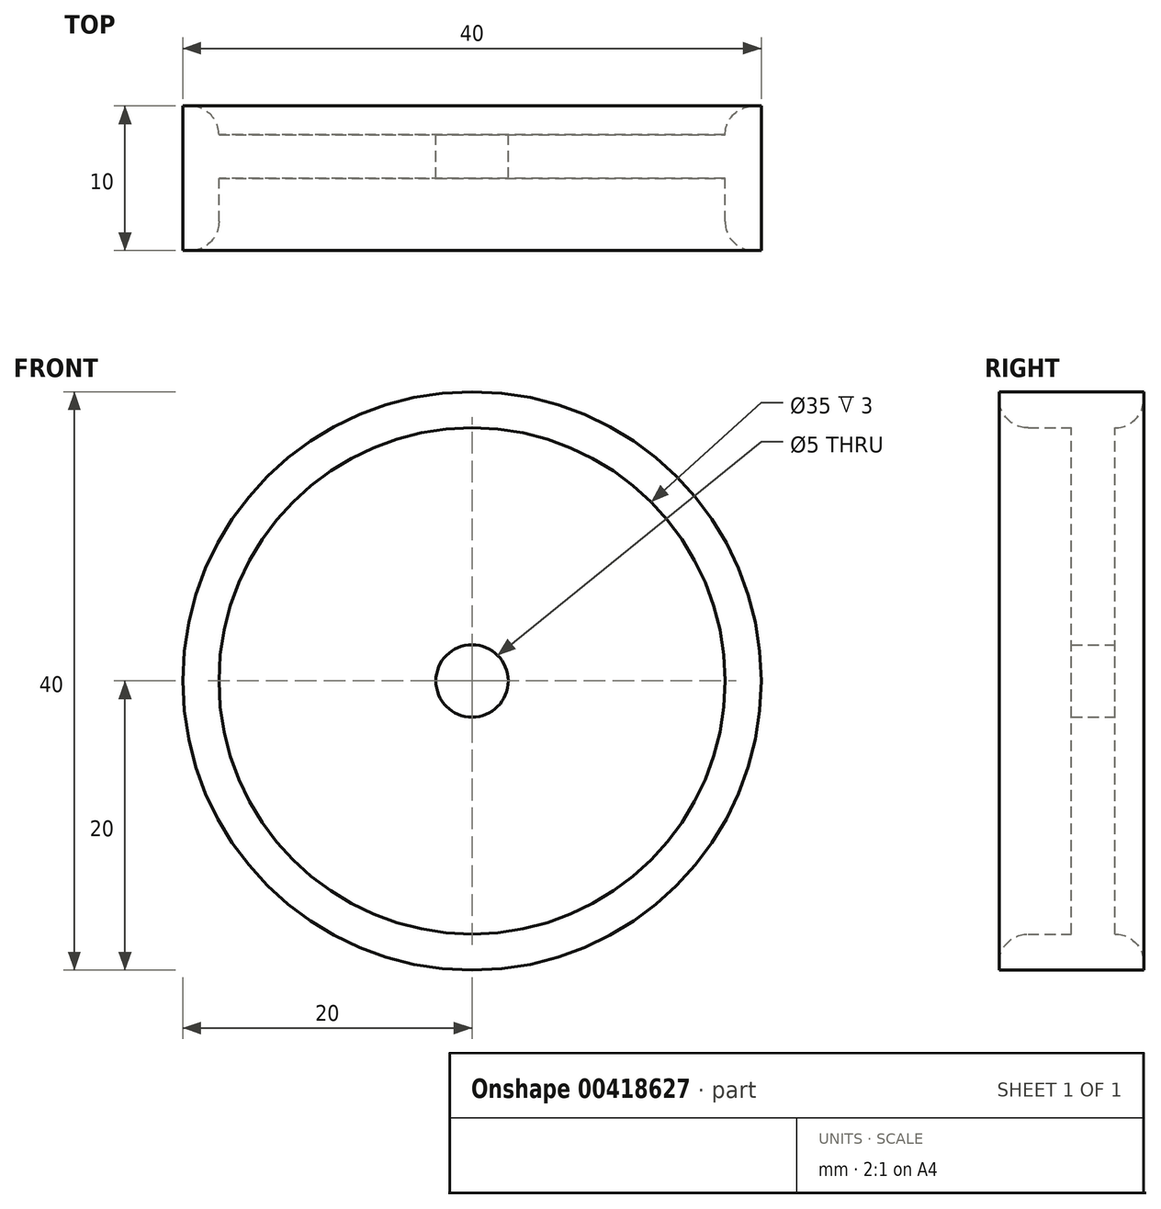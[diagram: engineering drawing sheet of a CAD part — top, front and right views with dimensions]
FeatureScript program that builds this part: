
annotation { "Feature Type Name" : "Feature", "Feature Type Description" : "" }
export const myFeature = defineFeature(function(context is Context, id is Id, definition is map)
    precondition{}
    {
        {
            var Q0;
            Q0=qCreatedBy(makeId("Front.planeOp"),FACE);
            var sketch = newSketch(context, id + "F0", { "sketchPlane" : qUnion([Q0])});
            skCircle(sketch, "E0", {"center": v(0, 0) * mm, "radius": 20 * mm});
            skCircle(sketch, "E1", {"center": v(0, 0) * mm, "radius": 17.5 * mm});
            skLineSegment(sketch, "E2", {"start": v(0, 0) * mm, "end": v(1.68, 17.42) * mm});
            skLineSegment(sketch, "E3.1.0", {"start": v(0, 0) * mm, "end": v(-17.42, 1.68) * mm});
            skLineSegment(sketch, "E3.2.0", {"start": v(0, 0) * mm, "end": v(-1.68, -17.42) * mm});
            skLineSegment(sketch, "E3.3.0", {"start": v(0, 0) * mm, "end": v(17.42, -1.68) * mm});
            skSolve(sketch);
        }
        {
            var Q0;
            Q0=makeQuery(id+"F0.imprint","IMPRINT",FACE,{"disambiguationData":[TD([[makeQuery(id+"F0.imprint","IMPRINT",EDGE,{"derivedFrom":sQuery(id+"F0.wireOp",EDGE,"E0")}),1.0]])]});
            extrude(context, id + "F1", {"entities" : qUnion([Q0]), "depth" : 10 * mm});
        }
        {
            var Q0;
            {var subQ0=sQuery(id+"F0.wireOp",EDGE,"E2");Q0=makeQuery(id+"F0.imprint","IMPRINT",FACE,{"disambiguationData":[TD([[makeQuery(id+"F0.imprint","IMPRINT",EDGE,{"derivedFrom":subQ0}),1.0]])]});}
            var Q1;
            {var subQ0=sQuery(id+"F0.wireOp",EDGE,"E3.2.0");Q1=makeQuery(id+"F0.imprint","IMPRINT",FACE,{"disambiguationData":[TD([[makeQuery(id+"F0.imprint","IMPRINT",EDGE,{"derivedFrom":subQ0}),1.0]])]});}
            var Q2;
            {var subQ0=sQuery(id+"F0.wireOp",EDGE,"E3.1.0");Q2=makeQuery(id+"F0.imprint","IMPRINT",FACE,{"disambiguationData":[TD([[makeQuery(id+"F0.imprint","IMPRINT",EDGE,{"derivedFrom":subQ0}),1.0]])]});}
            var Q3;
            {var subQ0=sQuery(id+"F0.wireOp",EDGE,"E2");Q3=makeQuery(id+"F0.imprint","IMPRINT",FACE,{"disambiguationData":[TD([[makeQuery(id+"F0.imprint","IMPRINT",EDGE,{"derivedFrom":subQ0}),-1.0]])]});}
            extrude(context, id + "F2", {"entities" : qUnion([Q0, Q1, Q2, Q3]), "operationType" : NewBodyOperationType.ADD, "depth" : 5 * mm, "hasSecondDirection" : true, "secondDirectionOppositeDirection" : true, "secondDirectionDepth" : -2 * mm});
        }
        {
            var Q0;
            Q0=makeQuery(id+"F1.opExtrude","CAP_EDGE",EDGE,{"disambiguationData":[OSD([sQuery(id+"F0.wireOp",EDGE,"E1")])],"isStart":false});
            var Q1;
            Q1=makeQuery(id+"F1.opExtrude","CAP_EDGE",EDGE,{"disambiguationData":[OSD([sQuery(id+"F0.wireOp",EDGE,"E1")])],"isStart":true});
            fillet(context, id + "F3", {"entities" : qUnion([Q0, Q1]), "radius" : 2 * mm, "tangentPropagation" : true, "allowEdgeOverflow" : false});
        }
        {
            var Q0;
            Q0=sQuery(id+"F0.wireOp",VERTEX,"E0.center");
            var Q1;
            Q1=makeQuery(id+"F1.opExtrude","SWEPT_BODY",BODY,{"disambiguationData":[OSD([sQuery(id+"F0.wireOp",EDGE,"E0"),sQuery(id+"F0.wireOp",EDGE,"E1")])]});
            hole(context, id + "F4", {"style" : HoleStyle.SIMPLE, "endStyle" : HoleEndStyle.THROUGH, "oppositeDirection" : true, "holeDiameter" : 5 * mm, "isTappedThrough" : true, "tappedDepth" : 12 * mm, "tapClearance" : 3, "locations" : qUnion([Q0]), "scope" : qUnion([Q1])});
        }
    });
